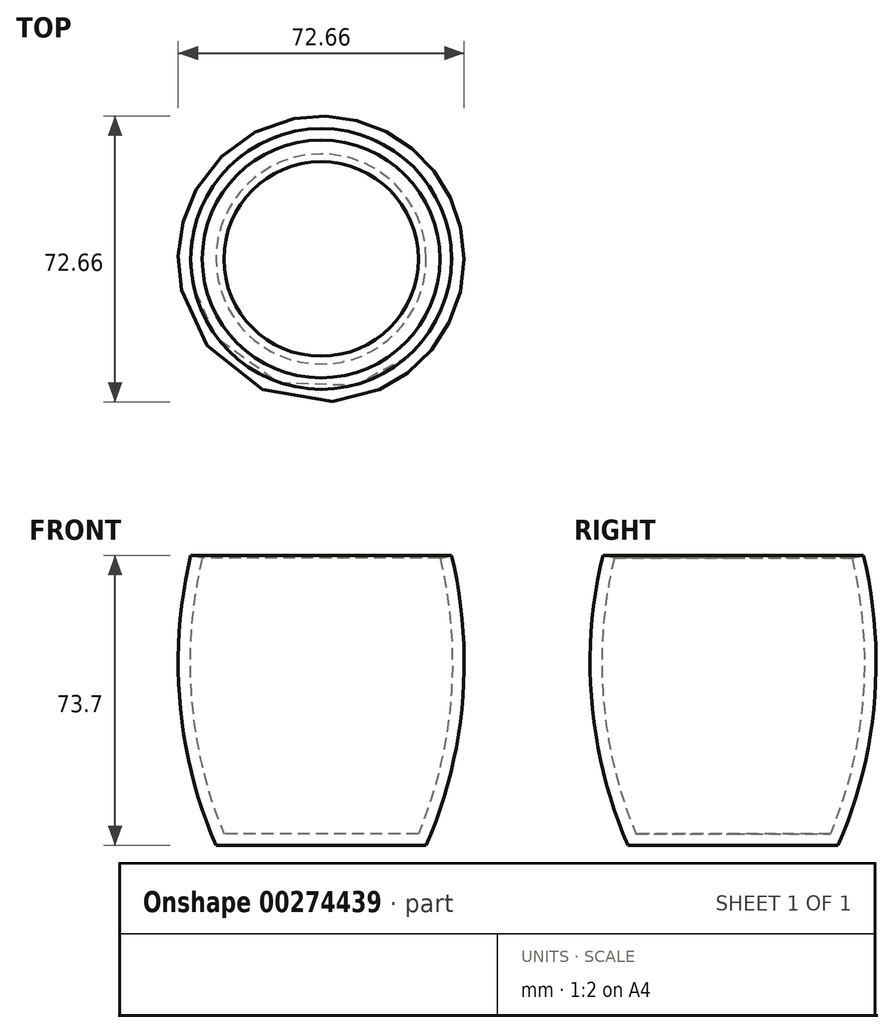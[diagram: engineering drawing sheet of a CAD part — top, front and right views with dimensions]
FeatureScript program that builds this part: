
annotation { "Feature Type Name" : "Feature", "Feature Type Description" : "" }
export const myFeature = defineFeature(function(context is Context, id is Id, definition is map)
    precondition{}
    {
        {
            var Q0;
            Q0=qCreatedBy(makeId("Front.planeOp"),FACE);
            var sketch = newSketch(context, id + "F0", { "sketchPlane" : qUnion([Q0])});
            skLineSegment(sketch, "E0", {"start": v(0, 0) * mm, "end": v(24.7, 0) * mm});
            skArc(sketch, "E1", {"start": v(24.7, 0) * mm, "mid": v(32.98, 34.57) * mm, "end": v(30.2, 70) * mm});
            skArc(sketch, "E2.0", {"start": v(26.7, -3) * mm, "mid": v(35.89, 33.33) * mm, "end": v(33.11, 70.7) * mm});
            skLineSegment(sketch, "E2.1", {"start": v(0, -3) * mm, "end": v(26.7, -3) * mm});
            skLineSegment(sketch, "E3", {"start": v(33.11, 70.7) * mm, "end": v(30.2, 70) * mm});
            skLineSegment(sketch, "E4", {"start": v(0, 0) * mm, "end": v(0, -3) * mm});
            skSolve(sketch);
        }
        {
            var Q0;
            Q0 = qSketchRegion(id + "F0", true);
            var Q1;
            Q1=sQuery(id+"F0.wireOp",EDGE,"E4");
            revolve(context, id + "F1", {"entities" : qUnion([Q0]), "axis" : qUnion([Q1]), "revolveType" : RevolveType.FULL});
        }
    });
